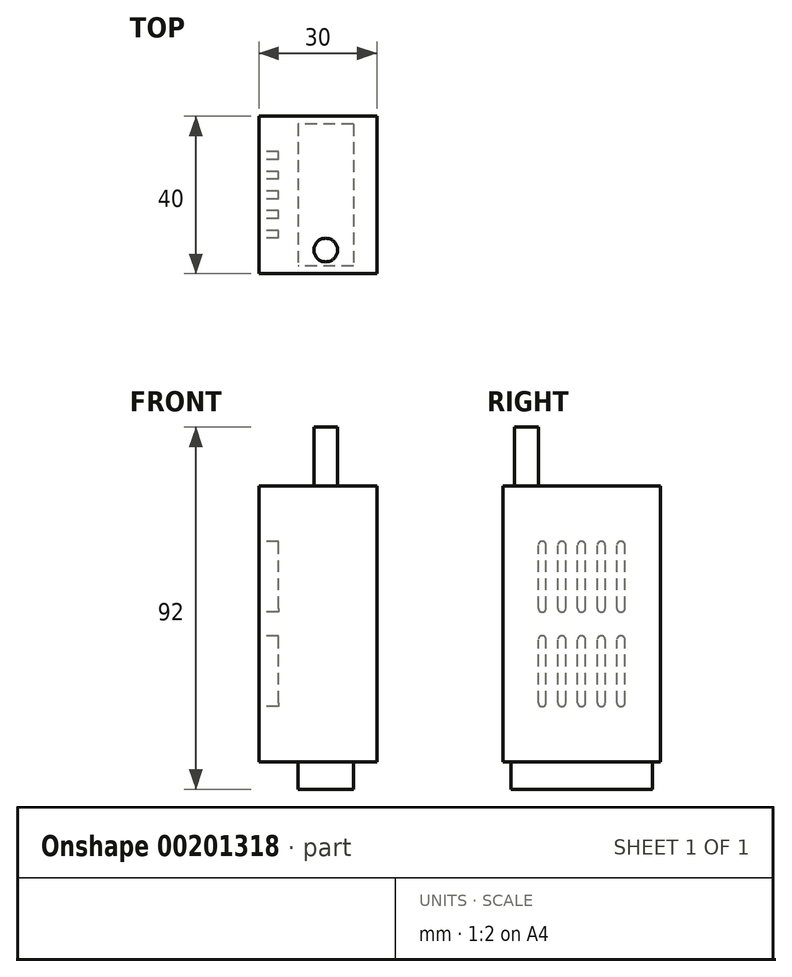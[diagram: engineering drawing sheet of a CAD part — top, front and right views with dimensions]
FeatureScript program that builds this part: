
annotation { "Feature Type Name" : "Feature", "Feature Type Description" : "" }
export const myFeature = defineFeature(function(context is Context, id is Id, definition is map)
    precondition{}
    {
        {
            var Q0;
            Q0=qCreatedBy(makeId("Top.planeOp"),FACE);
            var sketch = newSketch(context, id + "F0", { "sketchPlane" : qUnion([Q0])});
            skLineSegment(sketch, "E0.bottom", {"start": v(15, 20) * mm, "end": v(-15, 20) * mm});
            skLineSegment(sketch, "E0.top", {"start": v(15, -20) * mm, "end": v(-15, -20) * mm});
            skLineSegment(sketch, "E0.left", {"start": v(15, 20) * mm, "end": v(15, -20) * mm});
            skLineSegment(sketch, "E0.right", {"start": v(-15, 20) * mm, "end": v(-15, -20) * mm});
            skPoint(sketch, "E0.middle", {"position": v(0, 0) * mm});
            skLineSegment(sketch, "E1.bottom", {"start": v(9, 18) * mm, "end": v(-5, 18) * mm});
            skLineSegment(sketch, "E1.top", {"start": v(9, -18) * mm, "end": v(-5, -18) * mm});
            skLineSegment(sketch, "E1.left", {"start": v(9, 18) * mm, "end": v(9, -18) * mm});
            skLineSegment(sketch, "E1.right", {"start": v(-5, 18) * mm, "end": v(-5, -18) * mm});
            skPoint(sketch, "E1.middle", {"position": v(2, 0) * mm});
            skSolve(sketch);
        }
        {
            var Q0;
            Q0=makeQuery(id+"F0.imprint","IMPRINT",FACE,{"disambiguationData":[TD([[makeQuery(id+"F0.imprint","IMPRINT",EDGE,{"derivedFrom":sQuery(id+"F0.wireOp",EDGE,"E0.bottom")}),1.0]])]});
            var Q1;
            Q1=makeQuery(id+"F0.imprint","IMPRINT",FACE,{"disambiguationData":[TD([[makeQuery(id+"F0.imprint","IMPRINT",EDGE,{"derivedFrom":sQuery(id+"F0.wireOp",EDGE,"E1.bottom")}),1.0]])]});
            extrude(context, id + "F1", {"entities" : qUnion([Q0, Q1]), "depth" : 70 * mm});
        }
        {
            var Q0;
            Q0=makeQuery(id+"F0.imprint","IMPRINT",FACE,{"disambiguationData":[TD([[makeQuery(id+"F0.imprint","IMPRINT",EDGE,{"derivedFrom":sQuery(id+"F0.wireOp",EDGE,"E1.bottom")}),1.0]])]});
            extrude(context, id + "F2", {"entities" : qUnion([Q0]), "oppositeDirection" : true, "depth" : 7 * mm});
        }
        {
            var Q0;
            Q0=makeQuery(id+"F1.opExtrude","CAP_FACE",FACE,{"disambiguationData":[OSD([sQuery(id+"F0.wireOp",EDGE,"E0.bottom"),sQuery(id+"F0.wireOp",EDGE,"E0.top"),sQuery(id+"F0.wireOp",EDGE,"E0.left"),sQuery(id+"F0.wireOp",EDGE,"E0.right")])],"isStart":false});
            var sketch = newSketch(context, id + "F3", { "sketchPlane" : qUnion([Q0])});
            skCircle(sketch, "E2", {"center": v(2, -14) * mm, "radius": 3 * mm});
            skSolve(sketch);
        }
        {
            var Q0;
            Q0=makeQuery(id+"F3.imprint","IMPRINT",FACE,{"disambiguationData":[TD([[makeQuery(id+"F3.imprint","IMPRINT",EDGE,{"derivedFrom":sQuery(id+"F3.wireOp",EDGE,"E2")}),1.0]])]});
            extrude(context, id + "F4", {"entities" : qUnion([Q0]), "operationType" : NewBodyOperationType.ADD, "depth" : 15 * mm});
        }
        {
            var Q0;
            Q0=makeQuery(id+"F1.opExtrude","SWEPT_FACE",FACE,{"disambiguationData":[OSD([sQuery(id+"F0.wireOp",EDGE,"E0.right")])]});
            var sketch = newSketch(context, id + "F5", { "sketchPlane" : qUnion([Q0])});
            skCircle(sketch, "E3", {"center": v(10, 15) * mm, "radius": 1 * mm});
            skCircle(sketch, "E4.0.1.0", {"center": v(10, 31) * mm, "radius": 1 * mm});
            skLineSegment(sketch, "E4.direction1", {"start": v(10, 15) * mm, "end": v(21.41, 15) * mm, "construction": true});
            skLineSegment(sketch, "E4.direction2", {"start": v(10, 15) * mm, "end": v(10, 31) * mm, "construction": true});
            skLineSegment(sketch, "E5", {"start": v(11, 15) * mm, "end": v(11, 31) * mm});
            skLineSegment(sketch, "E6", {"start": v(9, 15) * mm, "end": v(9, 31) * mm});
            skCircle(sketch, "E7.0.1.0", {"center": v(10, 39) * mm, "radius": 1 * mm});
            skLineSegment(sketch, "E7.0.1.1", {"start": v(11, 39) * mm, "end": v(11, 55) * mm});
            skLineSegment(sketch, "E7.0.1.2", {"start": v(9, 39) * mm, "end": v(9, 55) * mm});
            skCircle(sketch, "E7.0.1.3", {"center": v(10, 55) * mm, "radius": 1 * mm});
            skCircle(sketch, "E7.1.0.0", {"center": v(5, 15) * mm, "radius": 1 * mm});
            skLineSegment(sketch, "E7.1.0.1", {"start": v(6, 15) * mm, "end": v(6, 31) * mm});
            skLineSegment(sketch, "E7.1.0.2", {"start": v(4, 15) * mm, "end": v(4, 31) * mm});
            skCircle(sketch, "E7.1.0.3", {"center": v(5, 31) * mm, "radius": 1 * mm});
            skCircle(sketch, "E7.1.1.0", {"center": v(5, 39) * mm, "radius": 1 * mm});
            skLineSegment(sketch, "E7.1.1.1", {"start": v(6, 39) * mm, "end": v(6, 55) * mm});
            skLineSegment(sketch, "E7.1.1.2", {"start": v(4, 39) * mm, "end": v(4, 55) * mm});
            skCircle(sketch, "E7.1.1.3", {"center": v(5, 55) * mm, "radius": 1 * mm});
            skCircle(sketch, "E7.2.0.0", {"center": v(0, 15) * mm, "radius": 1 * mm});
            skLineSegment(sketch, "E7.2.0.1", {"start": v(1, 15) * mm, "end": v(1, 31) * mm});
            skLineSegment(sketch, "E7.2.0.2", {"start": v(-1, 15) * mm, "end": v(-1, 31) * mm});
            skCircle(sketch, "E7.2.0.3", {"center": v(0, 31) * mm, "radius": 1 * mm});
            skCircle(sketch, "E7.2.1.0", {"center": v(0, 39) * mm, "radius": 1 * mm});
            skLineSegment(sketch, "E7.2.1.1", {"start": v(1, 39) * mm, "end": v(1, 55) * mm});
            skLineSegment(sketch, "E7.2.1.2", {"start": v(-1, 39) * mm, "end": v(-1, 55) * mm});
            skCircle(sketch, "E7.2.1.3", {"center": v(0, 55) * mm, "radius": 1 * mm});
            skCircle(sketch, "E7.3.0.0", {"center": v(-5, 15) * mm, "radius": 1 * mm});
            skLineSegment(sketch, "E7.3.0.1", {"start": v(-4, 15) * mm, "end": v(-4, 31) * mm});
            skLineSegment(sketch, "E7.3.0.2", {"start": v(-6, 15) * mm, "end": v(-6, 31) * mm});
            skCircle(sketch, "E7.3.0.3", {"center": v(-5, 31) * mm, "radius": 1 * mm});
            skCircle(sketch, "E7.3.1.0", {"center": v(-5, 39) * mm, "radius": 1 * mm});
            skLineSegment(sketch, "E7.3.1.1", {"start": v(-4, 39) * mm, "end": v(-4, 55) * mm});
            skLineSegment(sketch, "E7.3.1.2", {"start": v(-6, 39) * mm, "end": v(-6, 55) * mm});
            skCircle(sketch, "E7.3.1.3", {"center": v(-5, 55) * mm, "radius": 1 * mm});
            skCircle(sketch, "E7.4.0.0", {"center": v(-10, 15) * mm, "radius": 1 * mm});
            skLineSegment(sketch, "E7.4.0.1", {"start": v(-9, 15) * mm, "end": v(-9, 31) * mm});
            skLineSegment(sketch, "E7.4.0.2", {"start": v(-11, 15) * mm, "end": v(-11, 31) * mm});
            skCircle(sketch, "E7.4.0.3", {"center": v(-10, 31) * mm, "radius": 1 * mm});
            skCircle(sketch, "E7.4.1.0", {"center": v(-10, 39) * mm, "radius": 1 * mm});
            skLineSegment(sketch, "E7.4.1.1", {"start": v(-9, 39) * mm, "end": v(-9, 55) * mm});
            skLineSegment(sketch, "E7.4.1.2", {"start": v(-11, 39) * mm, "end": v(-11, 55) * mm});
            skCircle(sketch, "E7.4.1.3", {"center": v(-10, 55) * mm, "radius": 1 * mm});
            skLineSegment(sketch, "E7.direction1", {"start": v(10, 15) * mm, "end": v(5, 15) * mm, "construction": true});
            skLineSegment(sketch, "E7.direction2", {"start": v(10, 15) * mm, "end": v(10, 39) * mm, "construction": true});
            skSolve(sketch);
        }
        {
            var Q0;
            {var subQ0=sQuery(id+"F5.wireOp",EDGE,"E3");var subQ1=makeQuery(id+"F5.imprint","INTERSECT",VERTEX,{"derivedFrom":[subQ0,sQuery(id+"F5.wireOp",EDGE,"E5")]});Q0=makeQuery(id+"F5.imprint","IMPRINT",FACE,{"disambiguationData":[TD([[makeQuery(id+"F5.imprint","IMPRINT",EDGE,{"disambiguationData":[TD([[subQ1,-1.0]])],"derivedFrom":subQ0}),1.0]])]});}
            var Q1;
            {var subQ0=sQuery(id+"F5.wireOp",EDGE,"E5");Q1=makeQuery(id+"F5.imprint","IMPRINT",FACE,{"disambiguationData":[TD([[makeQuery(id+"F5.imprint","IMPRINT",EDGE,{"derivedFrom":subQ0}),1.0]])]});}
            var Q2;
            {var subQ0=sQuery(id+"F5.wireOp",EDGE,"E4.0.1.0");var subQ1=makeQuery(id+"F5.imprint","INTERSECT",VERTEX,{"derivedFrom":[subQ0,sQuery(id+"F5.wireOp",EDGE,"E5")]});Q2=makeQuery(id+"F5.imprint","IMPRINT",FACE,{"disambiguationData":[TD([[makeQuery(id+"F5.imprint","IMPRINT",EDGE,{"disambiguationData":[TD([[subQ1,-1.0]])],"derivedFrom":subQ0}),1.0]])]});}
            var Q3;
            {var subQ0=sQuery(id+"F5.wireOp",EDGE,"E7.0.1.3");var subQ1=makeQuery(id+"F5.imprint","INTERSECT",VERTEX,{"derivedFrom":[sQuery(id+"F5.wireOp",EDGE,"E7.0.1.1"),subQ0]});Q3=makeQuery(id+"F5.imprint","IMPRINT",FACE,{"disambiguationData":[TD([[makeQuery(id+"F5.imprint","IMPRINT",EDGE,{"disambiguationData":[TD([[subQ1,-1.0]])],"derivedFrom":subQ0}),1.0]])]});}
            var Q4;
            {var subQ0=sQuery(id+"F5.wireOp",EDGE,"E7.1.1.3");var subQ1=makeQuery(id+"F5.imprint","INTERSECT",VERTEX,{"derivedFrom":[sQuery(id+"F5.wireOp",EDGE,"E7.1.1.1"),subQ0]});Q4=makeQuery(id+"F5.imprint","IMPRINT",FACE,{"disambiguationData":[TD([[makeQuery(id+"F5.imprint","IMPRINT",EDGE,{"disambiguationData":[TD([[subQ1,-1.0]])],"derivedFrom":subQ0}),1.0]])]});}
            var Q5;
            {var subQ0=sQuery(id+"F5.wireOp",EDGE,"E7.2.1.3");var subQ1=makeQuery(id+"F5.imprint","INTERSECT",VERTEX,{"derivedFrom":[sQuery(id+"F5.wireOp",EDGE,"E7.2.1.1"),subQ0]});Q5=makeQuery(id+"F5.imprint","IMPRINT",FACE,{"disambiguationData":[TD([[makeQuery(id+"F5.imprint","IMPRINT",EDGE,{"disambiguationData":[TD([[subQ1,-1.0]])],"derivedFrom":subQ0}),1.0]])]});}
            var Q6;
            {var subQ0=sQuery(id+"F5.wireOp",EDGE,"E7.3.1.3");var subQ1=makeQuery(id+"F5.imprint","INTERSECT",VERTEX,{"derivedFrom":[sQuery(id+"F5.wireOp",EDGE,"E7.3.1.1"),subQ0]});Q6=makeQuery(id+"F5.imprint","IMPRINT",FACE,{"disambiguationData":[TD([[makeQuery(id+"F5.imprint","IMPRINT",EDGE,{"disambiguationData":[TD([[subQ1,-1.0]])],"derivedFrom":subQ0}),1.0]])]});}
            var Q7;
            {var subQ0=sQuery(id+"F5.wireOp",EDGE,"E7.4.1.3");var subQ1=makeQuery(id+"F5.imprint","INTERSECT",VERTEX,{"derivedFrom":[sQuery(id+"F5.wireOp",EDGE,"E7.4.1.1"),subQ0]});Q7=makeQuery(id+"F5.imprint","IMPRINT",FACE,{"disambiguationData":[TD([[makeQuery(id+"F5.imprint","IMPRINT",EDGE,{"disambiguationData":[TD([[subQ1,-1.0]])],"derivedFrom":subQ0}),1.0]])]});}
            var Q8;
            {var subQ0=sQuery(id+"F5.wireOp",EDGE,"E7.0.1.1");Q8=makeQuery(id+"F5.imprint","IMPRINT",FACE,{"disambiguationData":[TD([[makeQuery(id+"F5.imprint","IMPRINT",EDGE,{"derivedFrom":subQ0}),1.0]])]});}
            var Q9;
            {var subQ0=sQuery(id+"F5.wireOp",EDGE,"E7.1.1.1");Q9=makeQuery(id+"F5.imprint","IMPRINT",FACE,{"disambiguationData":[TD([[makeQuery(id+"F5.imprint","IMPRINT",EDGE,{"derivedFrom":subQ0}),1.0]])]});}
            var Q10;
            {var subQ0=sQuery(id+"F5.wireOp",EDGE,"E7.2.1.1");Q10=makeQuery(id+"F5.imprint","IMPRINT",FACE,{"disambiguationData":[TD([[makeQuery(id+"F5.imprint","IMPRINT",EDGE,{"derivedFrom":subQ0}),1.0]])]});}
            var Q11;
            {var subQ0=sQuery(id+"F5.wireOp",EDGE,"E7.3.1.1");Q11=makeQuery(id+"F5.imprint","IMPRINT",FACE,{"disambiguationData":[TD([[makeQuery(id+"F5.imprint","IMPRINT",EDGE,{"derivedFrom":subQ0}),1.0]])]});}
            var Q12;
            {var subQ0=sQuery(id+"F5.wireOp",EDGE,"E7.4.1.1");Q12=makeQuery(id+"F5.imprint","IMPRINT",FACE,{"disambiguationData":[TD([[makeQuery(id+"F5.imprint","IMPRINT",EDGE,{"derivedFrom":subQ0}),1.0]])]});}
            var Q13;
            {var subQ0=sQuery(id+"F5.wireOp",EDGE,"E7.0.1.0");var subQ1=makeQuery(id+"F5.imprint","INTERSECT",VERTEX,{"derivedFrom":[subQ0,sQuery(id+"F5.wireOp",EDGE,"E7.0.1.1")]});Q13=makeQuery(id+"F5.imprint","IMPRINT",FACE,{"disambiguationData":[TD([[makeQuery(id+"F5.imprint","IMPRINT",EDGE,{"disambiguationData":[TD([[subQ1,-1.0]])],"derivedFrom":subQ0}),1.0]])]});}
            var Q14;
            {var subQ0=sQuery(id+"F5.wireOp",EDGE,"E7.1.1.0");var subQ1=makeQuery(id+"F5.imprint","INTERSECT",VERTEX,{"derivedFrom":[subQ0,sQuery(id+"F5.wireOp",EDGE,"E7.1.1.1")]});Q14=makeQuery(id+"F5.imprint","IMPRINT",FACE,{"disambiguationData":[TD([[makeQuery(id+"F5.imprint","IMPRINT",EDGE,{"disambiguationData":[TD([[subQ1,-1.0]])],"derivedFrom":subQ0}),1.0]])]});}
            var Q15;
            {var subQ0=sQuery(id+"F5.wireOp",EDGE,"E7.2.1.0");var subQ1=makeQuery(id+"F5.imprint","INTERSECT",VERTEX,{"derivedFrom":[subQ0,sQuery(id+"F5.wireOp",EDGE,"E7.2.1.1")]});Q15=makeQuery(id+"F5.imprint","IMPRINT",FACE,{"disambiguationData":[TD([[makeQuery(id+"F5.imprint","IMPRINT",EDGE,{"disambiguationData":[TD([[subQ1,-1.0]])],"derivedFrom":subQ0}),1.0]])]});}
            var Q16;
            {var subQ0=sQuery(id+"F5.wireOp",EDGE,"E7.3.1.0");var subQ1=makeQuery(id+"F5.imprint","INTERSECT",VERTEX,{"derivedFrom":[subQ0,sQuery(id+"F5.wireOp",EDGE,"E7.3.1.1")]});Q16=makeQuery(id+"F5.imprint","IMPRINT",FACE,{"disambiguationData":[TD([[makeQuery(id+"F5.imprint","IMPRINT",EDGE,{"disambiguationData":[TD([[subQ1,-1.0]])],"derivedFrom":subQ0}),1.0]])]});}
            var Q17;
            {var subQ0=sQuery(id+"F5.wireOp",EDGE,"E7.4.1.0");var subQ1=makeQuery(id+"F5.imprint","INTERSECT",VERTEX,{"derivedFrom":[subQ0,sQuery(id+"F5.wireOp",EDGE,"E7.4.1.1")]});Q17=makeQuery(id+"F5.imprint","IMPRINT",FACE,{"disambiguationData":[TD([[makeQuery(id+"F5.imprint","IMPRINT",EDGE,{"disambiguationData":[TD([[subQ1,-1.0]])],"derivedFrom":subQ0}),1.0]])]});}
            var Q18;
            {var subQ0=sQuery(id+"F5.wireOp",EDGE,"E7.1.0.3");var subQ1=makeQuery(id+"F5.imprint","INTERSECT",VERTEX,{"derivedFrom":[sQuery(id+"F5.wireOp",EDGE,"E7.1.0.1"),subQ0]});Q18=makeQuery(id+"F5.imprint","IMPRINT",FACE,{"disambiguationData":[TD([[makeQuery(id+"F5.imprint","IMPRINT",EDGE,{"disambiguationData":[TD([[subQ1,-1.0]])],"derivedFrom":subQ0}),1.0]])]});}
            var Q19;
            {var subQ0=sQuery(id+"F5.wireOp",EDGE,"E7.2.0.3");var subQ1=makeQuery(id+"F5.imprint","INTERSECT",VERTEX,{"derivedFrom":[sQuery(id+"F5.wireOp",EDGE,"E7.2.0.1"),subQ0]});Q19=makeQuery(id+"F5.imprint","IMPRINT",FACE,{"disambiguationData":[TD([[makeQuery(id+"F5.imprint","IMPRINT",EDGE,{"disambiguationData":[TD([[subQ1,-1.0]])],"derivedFrom":subQ0}),1.0]])]});}
            var Q20;
            {var subQ0=sQuery(id+"F5.wireOp",EDGE,"E7.3.0.3");var subQ1=makeQuery(id+"F5.imprint","INTERSECT",VERTEX,{"derivedFrom":[sQuery(id+"F5.wireOp",EDGE,"E7.3.0.1"),subQ0]});Q20=makeQuery(id+"F5.imprint","IMPRINT",FACE,{"disambiguationData":[TD([[makeQuery(id+"F5.imprint","IMPRINT",EDGE,{"disambiguationData":[TD([[subQ1,-1.0]])],"derivedFrom":subQ0}),1.0]])]});}
            var Q21;
            {var subQ0=sQuery(id+"F5.wireOp",EDGE,"E7.4.0.3");var subQ1=makeQuery(id+"F5.imprint","INTERSECT",VERTEX,{"derivedFrom":[sQuery(id+"F5.wireOp",EDGE,"E7.4.0.1"),subQ0]});Q21=makeQuery(id+"F5.imprint","IMPRINT",FACE,{"disambiguationData":[TD([[makeQuery(id+"F5.imprint","IMPRINT",EDGE,{"disambiguationData":[TD([[subQ1,-1.0]])],"derivedFrom":subQ0}),1.0]])]});}
            var Q22;
            {var subQ0=sQuery(id+"F5.wireOp",EDGE,"E7.1.0.1");Q22=makeQuery(id+"F5.imprint","IMPRINT",FACE,{"disambiguationData":[TD([[makeQuery(id+"F5.imprint","IMPRINT",EDGE,{"derivedFrom":subQ0}),1.0]])]});}
            var Q23;
            {var subQ0=sQuery(id+"F5.wireOp",EDGE,"E7.2.0.1");Q23=makeQuery(id+"F5.imprint","IMPRINT",FACE,{"disambiguationData":[TD([[makeQuery(id+"F5.imprint","IMPRINT",EDGE,{"derivedFrom":subQ0}),1.0]])]});}
            var Q24;
            {var subQ0=sQuery(id+"F5.wireOp",EDGE,"E7.3.0.1");Q24=makeQuery(id+"F5.imprint","IMPRINT",FACE,{"disambiguationData":[TD([[makeQuery(id+"F5.imprint","IMPRINT",EDGE,{"derivedFrom":subQ0}),1.0]])]});}
            var Q25;
            {var subQ0=sQuery(id+"F5.wireOp",EDGE,"E7.4.0.1");Q25=makeQuery(id+"F5.imprint","IMPRINT",FACE,{"disambiguationData":[TD([[makeQuery(id+"F5.imprint","IMPRINT",EDGE,{"derivedFrom":subQ0}),1.0]])]});}
            var Q26;
            {var subQ0=sQuery(id+"F5.wireOp",EDGE,"E7.1.0.0");var subQ1=makeQuery(id+"F5.imprint","INTERSECT",VERTEX,{"derivedFrom":[subQ0,sQuery(id+"F5.wireOp",EDGE,"E7.1.0.1")]});Q26=makeQuery(id+"F5.imprint","IMPRINT",FACE,{"disambiguationData":[TD([[makeQuery(id+"F5.imprint","IMPRINT",EDGE,{"disambiguationData":[TD([[subQ1,-1.0]])],"derivedFrom":subQ0}),1.0]])]});}
            var Q27;
            {var subQ0=sQuery(id+"F5.wireOp",EDGE,"E7.2.0.0");var subQ1=makeQuery(id+"F5.imprint","INTERSECT",VERTEX,{"derivedFrom":[subQ0,sQuery(id+"F5.wireOp",EDGE,"E7.2.0.1")]});Q27=makeQuery(id+"F5.imprint","IMPRINT",FACE,{"disambiguationData":[TD([[makeQuery(id+"F5.imprint","IMPRINT",EDGE,{"disambiguationData":[TD([[subQ1,-1.0]])],"derivedFrom":subQ0}),1.0]])]});}
            var Q28;
            {var subQ0=sQuery(id+"F5.wireOp",EDGE,"E7.3.0.0");var subQ1=makeQuery(id+"F5.imprint","INTERSECT",VERTEX,{"derivedFrom":[subQ0,sQuery(id+"F5.wireOp",EDGE,"E7.3.0.1")]});Q28=makeQuery(id+"F5.imprint","IMPRINT",FACE,{"disambiguationData":[TD([[makeQuery(id+"F5.imprint","IMPRINT",EDGE,{"disambiguationData":[TD([[subQ1,-1.0]])],"derivedFrom":subQ0}),1.0]])]});}
            var Q29;
            {var subQ0=sQuery(id+"F5.wireOp",EDGE,"E7.4.0.0");var subQ1=makeQuery(id+"F5.imprint","INTERSECT",VERTEX,{"derivedFrom":[subQ0,sQuery(id+"F5.wireOp",EDGE,"E7.4.0.1")]});Q29=makeQuery(id+"F5.imprint","IMPRINT",FACE,{"disambiguationData":[TD([[makeQuery(id+"F5.imprint","IMPRINT",EDGE,{"disambiguationData":[TD([[subQ1,-1.0]])],"derivedFrom":subQ0}),1.0]])]});}
            extrude(context, id + "F6", {"entities" : qUnion([Q0, Q1, Q2, Q3, Q4, Q5, Q6, Q7, Q8, Q9, Q10, Q11, Q12, Q13, Q14, Q15, Q16, Q17, Q18, Q19, Q20, Q21, Q22, Q23, Q24, Q25, Q26, Q27, Q28, Q29]), "operationType" : NewBodyOperationType.REMOVE, "oppositeDirection" : true, "depth" : 5 * mm});
        }
    });
